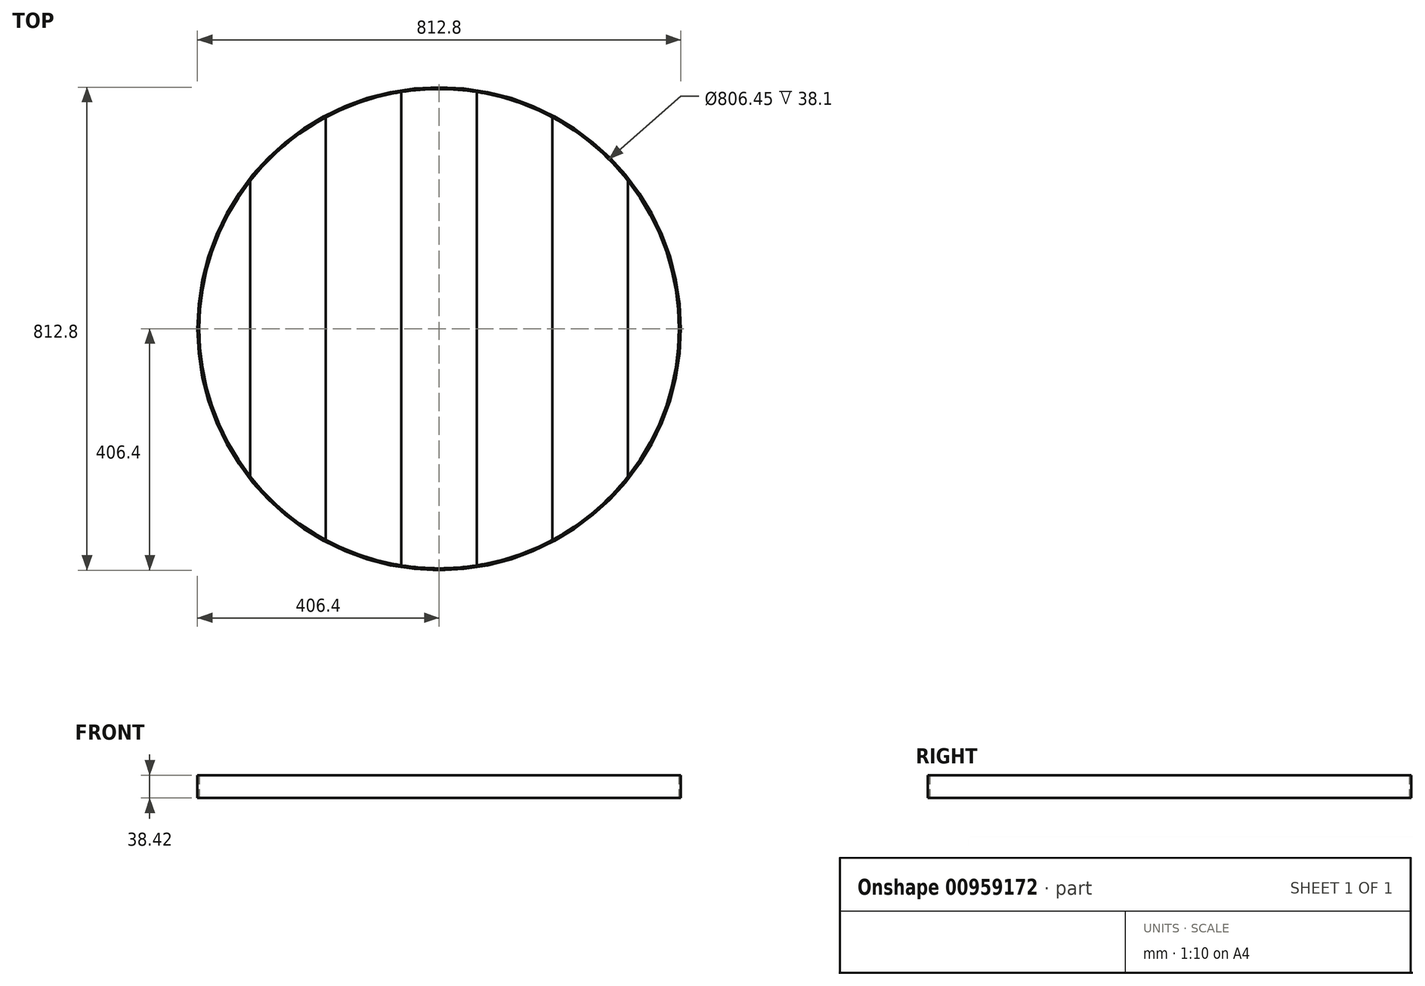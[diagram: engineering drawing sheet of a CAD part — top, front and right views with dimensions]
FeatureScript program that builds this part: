
annotation { "Feature Type Name" : "Feature", "Feature Type Description" : "" }
export const myFeature = defineFeature(function(context is Context, id is Id, definition is map)
    precondition{}
    {
        {
            var Q0;
            Q0=qCreatedBy(makeId("Top.planeOp"),FACE);
            var sketch = newSketch(context, id + "F0", { "sketchPlane" : qUnion([Q0])});
            skCircle(sketch, "E0", {"center": v(0, 0) * mm, "radius": 403.23 * mm});
            skCircle(sketch, "E1", {"center": v(0, 0) * mm, "radius": 406.4 * mm});
            skSolve(sketch);
        }
        {
            var Q0;
            Q0=makeQuery(id+"F0.imprint","IMPRINT",FACE,{"disambiguationData":[TD([[makeQuery(id+"F0.imprint","IMPRINT",EDGE,{"derivedFrom":sQuery(id+"F0.wireOp",EDGE,"E0")}),1.0]])]});
            extrude(context, id + "F1", {"entities" : qUnion([Q0]), "depth" : 38.1 * mm, "offsetDistance" : 25.4 * mm});
        }
        {
            var Q0;
            Q0=makeQuery(id+"F0.imprint","IMPRINT",FACE,{"disambiguationData":[TD([[makeQuery(id+"F0.imprint","IMPRINT",EDGE,{"derivedFrom":sQuery(id+"F0.wireOp",EDGE,"E0")}),-1.0]])]});
            extrude(context, id + "F2", {"entities" : qUnion([Q0]), "depth" : 38.1 * mm, "offsetDistance" : 25.4 * mm});
        }
        {
            var Q0;
            Q0=makeQuery(id+"F1.opExtrude","CAP_FACE",FACE,{"disambiguationData":[OSD([sQuery(id+"F0.wireOp",EDGE,"E0")])],"isStart":false});
            var sketch = newSketch(context, id + "F3", { "sketchPlane" : qUnion([Q0])});
            skLineSegment(sketch, "E2", {"start": v(0, 0) * mm, "end": v(0, -557.64) * mm, "construction": true});
            skLineSegment(sketch, "E3", {"start": v(-63.5, -398.2) * mm, "end": v(-63.5, 398.2) * mm});
            skLineSegment(sketch, "E4.MirrorCS", {"start": v(63.5, -398.2) * mm, "end": v(63.5, 398.2) * mm});
            skLineSegment(sketch, "E5.1.0.0", {"start": v(190.5, -355.39) * mm, "end": v(190.5, 355.39) * mm});
            skLineSegment(sketch, "E5.2.0.0", {"start": v(317.5, -248.56) * mm, "end": v(317.5, 248.56) * mm});
            skLineSegment(sketch, "E5.direction1", {"start": v(63.5, -398.2) * mm, "end": v(190.5, -398.2) * mm, "construction": true});
            skLineSegment(sketch, "E6.1.0.0", {"start": v(-190.5, -355.39) * mm, "end": v(-190.5, 355.39) * mm});
            skLineSegment(sketch, "E6.2.0.0", {"start": v(-317.5, -248.56) * mm, "end": v(-317.5, 248.56) * mm});
            skLineSegment(sketch, "E6.direction1", {"start": v(-63.5, -398.2) * mm, "end": v(-190.5, -398.2) * mm, "construction": true});
            skPoint(sketch, "E7", {"position": v(-190.5, 355.39) * mm});
            skPoint(sketch, "E8.orphan", {"position": v(-190.5, 398.2) * mm});
            skPoint(sketch, "E9", {"position": v(-317.5, 248.56) * mm});
            skPoint(sketch, "E10", {"position": v(190.5, 355.39) * mm});
            skPoint(sketch, "E11", {"position": v(317.5, 248.56) * mm});
            skPoint(sketch, "E12", {"position": v(317.5, -248.56) * mm});
            skPoint(sketch, "E13.orphan", {"position": v(317.5, -398.2) * mm});
            skPoint(sketch, "E14", {"position": v(190.5, -355.39) * mm});
            skPoint(sketch, "E15", {"position": v(-190.5, -355.39) * mm});
            skPoint(sketch, "E16", {"position": v(-317.5, -248.56) * mm});
            skPoint(sketch, "E17.orphan", {"position": v(-317.5, -398.2) * mm});
            skPoint(sketch, "E18.orphan", {"position": v(190.5, 398.2) * mm});
            skPoint(sketch, "E19.orphan", {"position": v(317.5, 398.2) * mm});
            skPoint(sketch, "E20.orphan", {"position": v(-317.5, 398.2) * mm});
            skSolve(sketch);
        }
        {
            var Q0;
            {var subQ0=sQuery(id+"F3.wireOp",EDGE,"E6.2.0.0");Q0=makeQuery(id+"F3.imprint","IMPRINT",FACE,{"disambiguationData":[TD([[makeQuery(id+"F3.imprint","IMPRINT",EDGE,{"derivedFrom":subQ0}),1.0]])]});}
            var Q1;
            {var subQ0=sQuery(id+"F3.wireOp",EDGE,"E3");Q1=makeQuery(id+"F3.imprint","IMPRINT",FACE,{"disambiguationData":[TD([[makeQuery(id+"F3.imprint","IMPRINT",EDGE,{"derivedFrom":subQ0}),1.0]])]});}
            var Q2;
            {var subQ0=sQuery(id+"F3.wireOp",EDGE,"E4.MirrorCS");Q2=makeQuery(id+"F3.imprint","IMPRINT",FACE,{"disambiguationData":[TD([[makeQuery(id+"F3.imprint","IMPRINT",EDGE,{"derivedFrom":subQ0}),-1.0]])]});}
            var Q3;
            {var subQ0=sQuery(id+"F3.wireOp",EDGE,"E5.2.0.0");Q3=makeQuery(id+"F3.imprint","IMPRINT",FACE,{"disambiguationData":[TD([[makeQuery(id+"F3.imprint","IMPRINT",EDGE,{"derivedFrom":subQ0}),-1.0]])]});}
            extrude(context, id + "F4", {"entities" : qUnion([Q0, Q1, Q2, Q3]), "depth" : 0.32 * mm, "offsetDistance" : 25.4 * mm});
        }
    });
